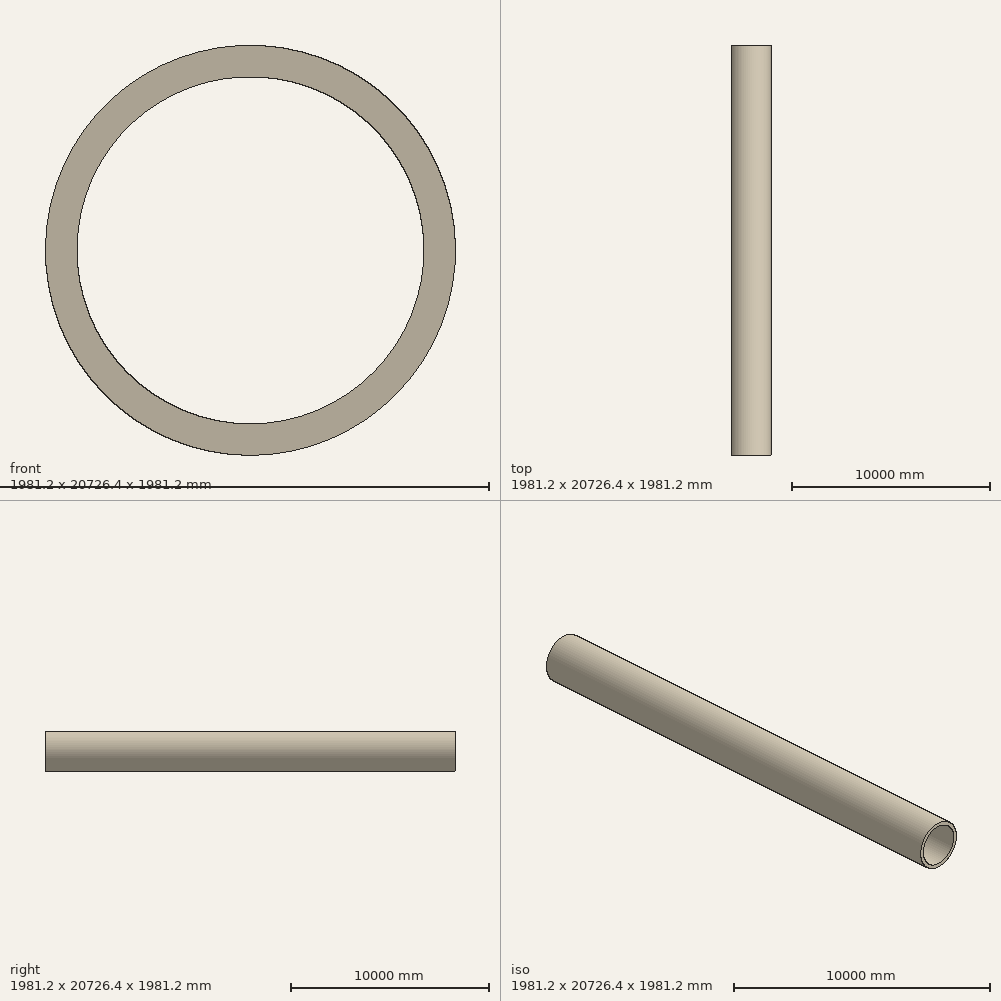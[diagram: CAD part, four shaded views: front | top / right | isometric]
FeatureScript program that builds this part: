
annotation { "Feature Type Name" : "Feature", "Feature Type Description" : "" }
export const myFeature = defineFeature(function(context is Context, id is Id, definition is map)
    precondition{}
    {
        {
            var Q0;
            Q0=qCreatedBy(makeId("Front.planeOp"),FACE);
            var sketch = newSketch(context, id + "F0", { "sketchPlane" : qUnion([Q0])});
            skCircle(sketch, "E0", {"center": v(0, 0) * mm, "radius": 990.6 * mm});
            skCircle(sketch, "E1", {"center": v(0, 0) * mm, "radius": 838.2 * mm});
            skSolve(sketch);
        }
        {
            var Q0;
            Q0=makeQuery(id+"F0.imprint","IMPRINT",FACE,{"disambiguationData":[TD([[makeQuery(id+"F0.imprint","IMPRINT",EDGE,{"derivedFrom":sQuery(id+"F0.wireOp",EDGE,"E0")}),1.0]])]});
            extrude(context, id + "F1", {"entities" : qUnion([Q0]), "depth" : 20726.4 * mm});
        }
    });
